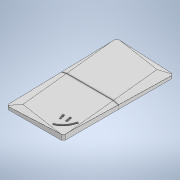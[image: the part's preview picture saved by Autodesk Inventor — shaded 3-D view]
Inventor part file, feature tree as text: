
AUTODESK INVENTOR PART (.ipt)
format: ipt  version: 2020 (Build 240168000, 168)  size: 580,608 bytes
history: native  units: mm
features: sketch x17, extrude x10, plane x6, other x5, pattern_circular x3, fillet x3, move_body x3, sweep x2, chamfer x1, boolean_combine x1, projected_geometry x1
ambient origin geometry x8: Origin, YZ Plane, XZ Plane, XY Plane, X Axis, Y Axis, Z Axis, Center Point
bodies: Solid1 (feature_tree), Solid3 (feature_tree)
feature tree (52):
  other  "Grin.ipt"
  extrude  "Extrusion1"  Depth=85.0mm
  extrude  "Extrusion2"  Depth=5.0mm
  extrude  "Extrusion3"  Depth=4.0mm TaperAngle=0.0deg
  sketch  "Sketch4"  dims[d9=15.0mm d10=10.0mm]
  sketch  "Sketch5"  dims[d13=8.2mm d14=4.0mm]
  sketch  "Sketch6"  dims[d15=10.0mm d16=0.0mm]
  plane  "Work Plane1"
  extrude  "Extrusion4"  Depth=10.0mm
  sketch  "Sketch8"  dims[d18=6.245mm d19=0.0mm d20=20.0mm d21=360.0deg d23=3.0mm d24=2.0mm d25=45.0deg d26=0.1mm]
  plane  "Work Plane2"
  extrude  "Extrusion5"  Depth=4.0mm
  pattern_circular  "Circular Pattern1"  Count=2 Angle=360.0deg
  chamfer  "Chamfer1"  Distance=3.0mm Angle=45.0deg
  fillet  "Fillet1"  Radius=0.1mm
  sketch  "Sketch10"  dims[d29=20.0mm d31=0.75mm d32=20.0mm d34=0.75mm d37=60.0mm d39=360.0deg]
  extrude  "Extrusion9"  Depth=8.828363mm
  move_body  "Move Body4"
  move_body  "Move Body5"
  move_body  "Move Body6"
  boolean_combine  "Combine1"
  fillet  "Fillet3"  Radius=60.0mm
  extrude  "Extrusion10"  Depth=1.5mm TaperAngle=0.0deg
  extrude  "Extrusion6"  Depth=1.0mm TaperAngle=0.0deg
  pattern_circular  "Circular Pattern2"  [2 undecoded]
  extrude  "Extrusion7"  Depth=10.0mm
  plane  "Work Plane4"
  sketch  "Sketch11"  dims[d41=1.5mm d42=1.0mm d43=0.0mm]
  extrude  "Extrusion8"  TaperAngle=0.0deg  [1 undecoded]
  sweep  "Sweep1"
  pattern_circular  "Circular Pattern3"  [2 undecoded]
  fillet  "Fillet2"  [1 undecoded]
  other  "Work Point1"
  other  "Work Point2"
  plane  "Work Plane5"
  sketch  "Sketch14"  dims[d50=4.5mm]
  plane  "Work Plane6"
  sweep  "Sweep2"
  sketch  "Sketch1"  dims[d0=165.0mm d1=85.0mm]
  sketch  "Sketch2"  dims[d2=2.0mm d3=0.0mm d4=5.0mm]
  projected_geometry  "Projected Loop1"
  sketch  "Sketch3"  dims[d5=2.0mm d6=0.0mm d7=4.0mm d8=0.0mm]
  sketch  "Sketch7"  dims[d17=8.2mm]
  sketch  "Sketch9"  dims[d27=29.427878mm d28=8.828363mm]
  plane  "Work Plane3"
  sketch  "Sketch12"  dims[d44=60.0mm d45=360.0deg d47=1.0mm d48=0.0mm]
  sketch  "Sketch13"  dims[d49=90.0deg]
  sketch  "Sketch15"  dims[d51=4.5mm]
  sketch  "Sketch16"  dims[d52=22.75mm d53=4.25mm d54=0.0mm d55=0.0mm]
  other  "Solid1::Grin.ipt_1"
  other  "TaggingFeature2"
  sketch  "Sketch17"  dims[d56=1.5mm d57=0.75mm d58=0.75mm d59=0.0mm d60=0.0mm d61=20.0mm d62=360.0deg d64=0.1mm d65=90.0deg d66=1.0mm d67=1.0mm d68=0.0mm d69=0.0mm d70=1.5mm d71=1.0mm d72=4.5mm d73=1.0mm d74=0.0mm d75=0.0mm d84=25.0mm d85=-15.707963mm d86=10.0mm d87=0.0mm d88=0.0mm d89=0.0mm d90=6.5mm d91=0.0mm d92=17.0mm d93=0.0mm d94=65.0mm d95=0.3mm d96=6.981317mm d97=1.5mm d98=0.5mm d99=0.5mm d100=10.0mm d101=0.0mm]
note: 6 required parameter values undecoded (feature->parameter linkage not recoverable at this tier; creation-order binding heuristic only, values carry confidence <= 0.55)
